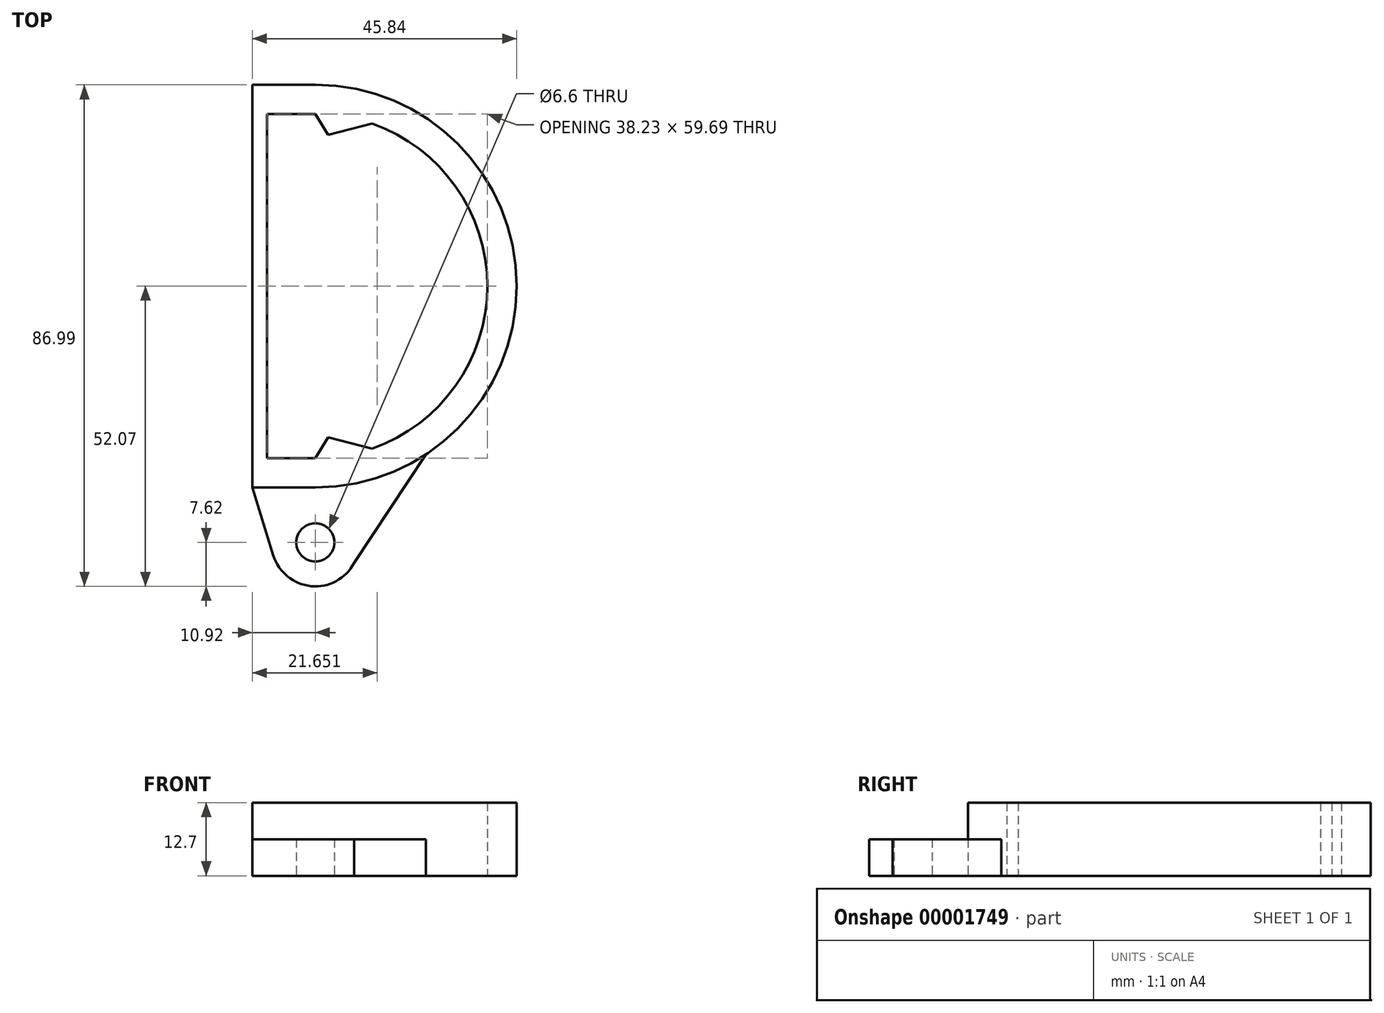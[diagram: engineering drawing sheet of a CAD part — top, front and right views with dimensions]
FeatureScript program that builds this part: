
annotation { "Feature Type Name" : "Feature", "Feature Type Description" : "" }
export const myFeature = defineFeature(function(context is Context, id is Id, definition is map)
    precondition{}
    {
        {
            var Q0;
            Q0=qCreatedBy(makeId("Top.planeOp"),FACE);
            var sketch = newSketch(context, id + "F0", { "sketchPlane" : qUnion([Q0])});
            skArc(sketch, "E0", {"start": v(0, -29.85) * mm, "mid": v(29.85, 0) * mm, "end": v(0, 29.85) * mm});
            skArc(sketch, "E1", {"start": v(0, -34.93) * mm, "mid": v(34.93, 0) * mm, "end": v(0, 34.93) * mm});
            skLineSegment(sketch, "E2", {"start": v(0, 34.93) * mm, "end": v(0, -34.93) * mm, "construction": true});
            skLineSegment(sketch, "E3", {"start": v(0, 34.93) * mm, "end": v(-10.92, 34.93) * mm});
            skLineSegment(sketch, "E4", {"start": v(-10.92, 34.93) * mm, "end": v(-10.92, -34.93) * mm});
            skLineSegment(sketch, "E5", {"start": v(-10.92, -34.93) * mm, "end": v(0, -34.93) * mm});
            skLineSegment(sketch, "E6", {"start": v(0, 29.85) * mm, "end": v(-8.38, 29.85) * mm});
            skLineSegment(sketch, "E7", {"start": v(-8.38, 29.85) * mm, "end": v(-8.38, -29.85) * mm});
            skLineSegment(sketch, "E8", {"start": v(-8.38, -29.85) * mm, "end": v(0, -29.85) * mm});
            skLineSegment(sketch, "E9", {"start": v(0, 29.85) * mm, "end": v(2.24, 26.22) * mm});
            skLineSegment(sketch, "E10", {"start": v(2.24, 26.22) * mm, "end": v(9.84, 28.18) * mm});
            skLineSegment(sketch, "E11", {"start": v(6.33, 0) * mm, "end": v(0, 0) * mm, "construction": true});
            skLineSegment(sketch, "E12.0.MirrorCS", {"start": v(2.24, -26.22) * mm, "end": v(9.84, -28.18) * mm});
            skLineSegment(sketch, "E13.0.MirrorCS", {"start": v(0, -29.85) * mm, "end": v(2.24, -26.22) * mm});
            skSolve(sketch);
        }
        {
            var Q0;
            Q0=makeQuery(id+"F0.imprint","IMPRINT",FACE,{"disambiguationData":[TD([[makeQuery(id+"F0.imprint","IMPRINT",EDGE,{"derivedFrom":sQuery(id+"F0.wireOp",EDGE,"E1")}),1.0]])]});
            var Q1;
            {var subQ1=sQuery(id+"F0.wireOp",EDGE,"E9");Q1=makeQuery(id+"F0.imprint","IMPRINT",FACE,{"disambiguationData":[TD([[makeQuery(id+"F0.imprint","IMPRINT",EDGE,{"derivedFrom":subQ1}),1.0]])]});}
            var Q2;
            {var subQ1=sQuery(id+"F0.wireOp",EDGE,"E12.0.MirrorCS");Q2=makeQuery(id+"F0.imprint","IMPRINT",FACE,{"disambiguationData":[TD([[makeQuery(id+"F0.imprint","IMPRINT",EDGE,{"derivedFrom":subQ1}),-1.0]])]});}
            extrude(context, id + "F1", {"entities" : qUnion([Q0, Q1, Q2]), "depth" : 12.7 * mm});
        }
        {
            var Q0;
            Q0=qCreatedBy(makeId("Top.planeOp"),FACE);
            var sketch = newSketch(context, id + "F2", { "sketchPlane" : qUnion([Q0])});
            skLineSegment(sketch, "E14", {"start": v(0, 0) * mm, "end": v(0, -44.45) * mm, "construction": true});
            skCircle(sketch, "E15", {"center": v(0, -44.45) * mm, "radius": 3.3 * mm});
            skSolve(sketch);
        }
        {
            var Q0;
            Q0=qCreatedBy(makeId("Top.planeOp"),FACE);
            var sketch = newSketch(context, id + "F3", { "sketchPlane" : qUnion([Q0])});
            skCircle(sketch, "E16", {"center": v(0, -44.45) * mm, "radius": 7.62 * mm});
            skLineSegment(sketch, "E17", {"start": v(-10.92, -34.93) * mm, "end": v(-7.28, -46.7) * mm});
            skLineSegment(sketch, "E18", {"start": v(6.73, -48.03) * mm, "end": v(19.2, -29.18) * mm});
            skLineSegment(sketch, "E19", {"start": v(19.2, -29.18) * mm, "end": v(-10.92, -34.93) * mm});
            skSolve(sketch);
        }
        {
            var Q0;
            {var subQ1=sQuery(id+"F3.wireOp",EDGE,"E17");Q0=makeQuery(id+"F3.imprint","IMPRINT",FACE,{"disambiguationData":[TD([[makeQuery(id+"F3.imprint","IMPRINT",EDGE,{"derivedFrom":subQ1}),1.0]])]});}
            var Q1;
            {var subQ0=sQuery(id+"F3.wireOp",EDGE,"E16");var subQ2=makeQuery(id+"F3.imprint","INTERSECT",VERTEX,{"derivedFrom":[subQ0,sQuery(id+"F3.wireOp",EDGE,"E17")]});Q1=makeQuery(id+"F3.imprint","IMPRINT",FACE,{"disambiguationData":[TD([[makeQuery(id+"F3.imprint","IMPRINT",EDGE,{"disambiguationData":[TD([[subQ2,-1.0]])],"derivedFrom":subQ0}),1.0]])]});}
            extrude(context, id + "F4", {"entities" : qUnion([Q0, Q1]), "operationType" : NewBodyOperationType.ADD, "depth" : 6.35 * mm});
        }
        {
            var Q0;
            Q0 = qSketchRegion(id + "F2", true);
            extrude(context, id + "F5", {"entities" : qUnion([Q0]), "operationType" : NewBodyOperationType.REMOVE, "depth" : 6.35 * mm});
        }
    });
